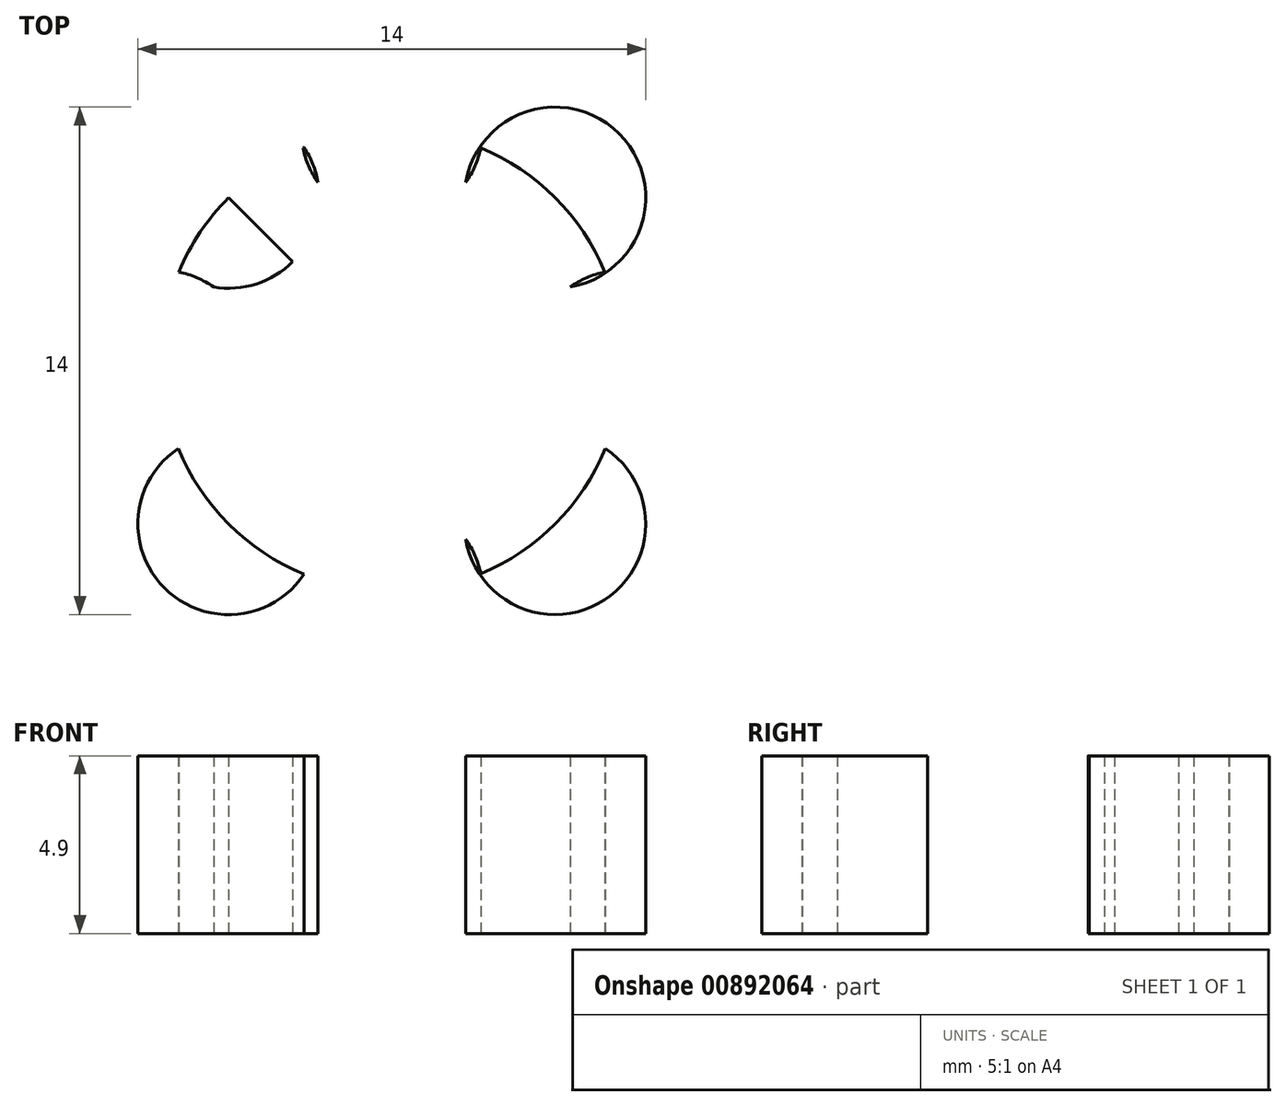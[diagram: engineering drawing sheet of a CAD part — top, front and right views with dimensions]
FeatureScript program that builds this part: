
annotation { "Feature Type Name" : "Feature", "Feature Type Description" : "" }
export const myFeature = defineFeature(function(context is Context, id is Id, definition is map)
    precondition{}
    {
        {
            var Q0;
            Q0=qCreatedBy(makeId("Top.planeOp"),FACE);
            var sketch = newSketch(context, id + "F0", { "sketchPlane" : qUnion([Q0])});
            skCircle(sketch, "E0", {"center": v(0, 0) * mm, "radius": 6.37 * mm});
            skArc(sketch, "E1", {"start": v(2.45, 5.88) * mm, "mid": v(0, 3.87) * mm, "end": v(-2.45, 5.88) * mm});
            skArc(sketch, "E2.1.0", {"start": v(5.88, -2.45) * mm, "mid": v(3.87, 0) * mm, "end": v(5.88, 2.45) * mm});
            skArc(sketch, "E2.2.0", {"start": v(-2.45, -5.88) * mm, "mid": v(0, -3.87) * mm, "end": v(2.45, -5.88) * mm});
            skArc(sketch, "E2.3.0", {"start": v(-5.88, 2.45) * mm, "mid": v(-3.87, 0) * mm, "end": v(-5.88, -2.45) * mm});
            skLineSegment(sketch, "E2.anchor1", {"start": v(0, 0) * mm, "end": v(-2.45, 5.88) * mm, "construction": true});
            skLineSegment(sketch, "E2.anchor2", {"start": v(0, 0) * mm, "end": v(-5.88, -2.45) * mm, "construction": true});
            skLineSegment(sketch, "E3", {"start": v(0, 0) * mm, "end": v(-5.34, 5.34) * mm});
            skCircle(sketch, "E4", {"center": v(-4.5, 4.5) * mm, "radius": 2.5 * mm});
            skCircle(sketch, "E5.1.0", {"center": v(-4.5, -4.5) * mm, "radius": 2.5 * mm});
            skCircle(sketch, "E5.2.0", {"center": v(4.5, -4.5) * mm, "radius": 2.5 * mm});
            skCircle(sketch, "E5.3.0", {"center": v(4.5, 4.5) * mm, "radius": 2.5 * mm});
            skSolve(sketch);
        }
        {
            var Q0;
            {var subQ0=sQuery(id+"F0.wireOp",EDGE,"E0");var subQ5=makeQuery(id+"F0.imprint","INTERSECT",VERTEX,{"disambiguationData":[OD(1.0)],"derivedFrom":[subQ0,sQuery(id+"F0.wireOp",EDGE,"E1")]});Q0=makeQuery(id+"F0.imprint","IMPRINT",FACE,{"disambiguationData":[TD([[makeQuery(id+"F0.imprint","IMPRINT",EDGE,{"disambiguationData":[TD([[subQ5,1.0]])],"derivedFrom":subQ0}),-1.0]])]});}
            var Q1;
            {var subQ0=sQuery(id+"F0.wireOp",EDGE,"E0");var subQ1=makeQuery(id+"F0.imprint","INTERSECT",VERTEX,{"disambiguationData":[OD(1.0)],"derivedFrom":[subQ0,sQuery(id+"F0.wireOp",EDGE,"E2.1.0")]});Q1=makeQuery(id+"F0.imprint","IMPRINT",FACE,{"disambiguationData":[TD([[makeQuery(id+"F0.imprint","IMPRINT",EDGE,{"disambiguationData":[TD([[subQ1,1.0]])],"derivedFrom":subQ0}),-1.0]])]});}
            var Q2;
            {var subQ9=sQuery(id+"F0.wireOp",EDGE,"E5.3.0");var subQ10=sQuery(id+"F0.wireOp",EDGE,"E1");var subQ11=makeQuery(id+"F0.imprint","INTERSECT",VERTEX,{"derivedFrom":[subQ10,subQ9]});Q2=makeQuery(id+"F0.imprint","IMPRINT",FACE,{"disambiguationData":[TD([[makeQuery(id+"F0.imprint","IMPRINT",EDGE,{"disambiguationData":[TD([[subQ11,-1.0]])],"derivedFrom":subQ10}),1.0]])]});}
            var Q3;
            {var subQ0=sQuery(id+"F0.wireOp",EDGE,"E0");var subQ1=makeQuery(id+"F0.imprint","INTERSECT",VERTEX,{"disambiguationData":[OD(1.0)],"derivedFrom":[subQ0,sQuery(id+"F0.wireOp",EDGE,"E2.2.0")]});Q3=makeQuery(id+"F0.imprint","IMPRINT",FACE,{"disambiguationData":[TD([[makeQuery(id+"F0.imprint","IMPRINT",EDGE,{"disambiguationData":[TD([[subQ1,1.0]])],"derivedFrom":subQ0}),-1.0]])]});}
            var Q4;
            {var subQ0=sQuery(id+"F0.wireOp",EDGE,"E0");var subQ1=makeQuery(id+"F0.imprint","INTERSECT",VERTEX,{"disambiguationData":[OD(1.0)],"derivedFrom":[subQ0,sQuery(id+"F0.wireOp",EDGE,"E2.3.0")]});Q4=makeQuery(id+"F0.imprint","IMPRINT",FACE,{"disambiguationData":[TD([[makeQuery(id+"F0.imprint","IMPRINT",EDGE,{"disambiguationData":[TD([[subQ1,1.0]])],"derivedFrom":subQ0}),-1.0]])]});}
            var Q5;
            {var subQ0=sQuery(id+"F0.wireOp",EDGE,"E1");var subQ1=sQuery(id+"F0.wireOp",EDGE,"E0");var subQ2=makeQuery(id+"F0.imprint","INTERSECT",VERTEX,{"disambiguationData":[OD(0.0)],"derivedFrom":[subQ1,subQ0]});Q5=makeQuery(id+"F0.imprint","IMPRINT",FACE,{"disambiguationData":[TD([[makeQuery(id+"F0.imprint","IMPRINT",EDGE,{"disambiguationData":[TD([[subQ2,1.0]])],"derivedFrom":subQ1}),1.0]])]});}
            var Q6;
            {var subQ0=sQuery(id+"F0.wireOp",EDGE,"E2.3.0");var subQ1=sQuery(id+"F0.wireOp",EDGE,"E0");var subQ2=makeQuery(id+"F0.imprint","INTERSECT",VERTEX,{"disambiguationData":[OD(0.0)],"derivedFrom":[subQ1,subQ0]});Q6=makeQuery(id+"F0.imprint","IMPRINT",FACE,{"disambiguationData":[TD([[makeQuery(id+"F0.imprint","IMPRINT",EDGE,{"disambiguationData":[TD([[subQ2,1.0]])],"derivedFrom":subQ1}),1.0]])]});}
            var Q7;
            {var subQ0=sQuery(id+"F0.wireOp",EDGE,"E2.2.0");var subQ1=sQuery(id+"F0.wireOp",EDGE,"E0");var subQ2=makeQuery(id+"F0.imprint","INTERSECT",VERTEX,{"disambiguationData":[OD(0.0)],"derivedFrom":[subQ1,subQ0]});Q7=makeQuery(id+"F0.imprint","IMPRINT",FACE,{"disambiguationData":[TD([[makeQuery(id+"F0.imprint","IMPRINT",EDGE,{"disambiguationData":[TD([[subQ2,1.0]])],"derivedFrom":subQ1}),1.0]])]});}
            var Q8;
            {var subQ0=sQuery(id+"F0.wireOp",EDGE,"E1");var subQ1=sQuery(id+"F0.wireOp",EDGE,"E0");var subQ2=makeQuery(id+"F0.imprint","INTERSECT",VERTEX,{"disambiguationData":[OD(1.0)],"derivedFrom":[subQ1,subQ0]});Q8=makeQuery(id+"F0.imprint","IMPRINT",FACE,{"disambiguationData":[TD([[makeQuery(id+"F0.imprint","IMPRINT",EDGE,{"disambiguationData":[TD([[subQ2,-1.0]])],"derivedFrom":subQ1}),1.0]])]});}
            var Q9;
            {var subQ0=sQuery(id+"F0.wireOp",EDGE,"E2.1.0");var subQ1=sQuery(id+"F0.wireOp",EDGE,"E0");var subQ2=makeQuery(id+"F0.imprint","INTERSECT",VERTEX,{"disambiguationData":[OD(0.0)],"derivedFrom":[subQ1,subQ0]});Q9=makeQuery(id+"F0.imprint","IMPRINT",FACE,{"disambiguationData":[TD([[makeQuery(id+"F0.imprint","IMPRINT",EDGE,{"disambiguationData":[TD([[subQ2,1.0]])],"derivedFrom":subQ1}),1.0]])]});}
            extrude(context, id + "F1", {"entities" : qUnion([Q0, Q1, Q2, Q3, Q4, Q5, Q6, Q7, Q8, Q9]), "depth" : 4.9 * mm, "offsetDistance" : 25 * mm});
        }
        {
            var Q0;
            Q0=sQuery(id+"F0.wireOp",VERTEX,"E0.center");
            var Q1;
            Q1=makeQuery(id+"F1.opExtrude","SWEPT_BODY",BODY,{"disambiguationData":[OSD([sQuery(id+"F0.wireOp",EDGE,"E0"),sQuery(id+"F0.wireOp",EDGE,"E1"),sQuery(id+"F0.wireOp",EDGE,"E2.1.0"),sQuery(id+"F0.wireOp",EDGE,"E2.2.0"),sQuery(id+"F0.wireOp",EDGE,"E2.3.0"),sQuery(id+"F0.wireOp",EDGE,"E4"),sQuery(id+"F0.wireOp",EDGE,"E5.1.0"),sQuery(id+"F0.wireOp",EDGE,"E5.2.0"),sQuery(id+"F0.wireOp",EDGE,"E5.3.0")])]});
            hole(context, id + "F2", {"style" : HoleStyle.SIMPLE, "endStyle" : HoleEndStyle.THROUGH, "oppositeDirection" : true, "holeDiameter" : 3.5 * mm, "majorDiameter" : 5 * mm, "isTappedThrough" : true, "tappedDepth" : 12 * mm, "tapClearance" : 3, "locations" : qUnion([Q0]), "scope" : qUnion([Q1])});
        }
    });
